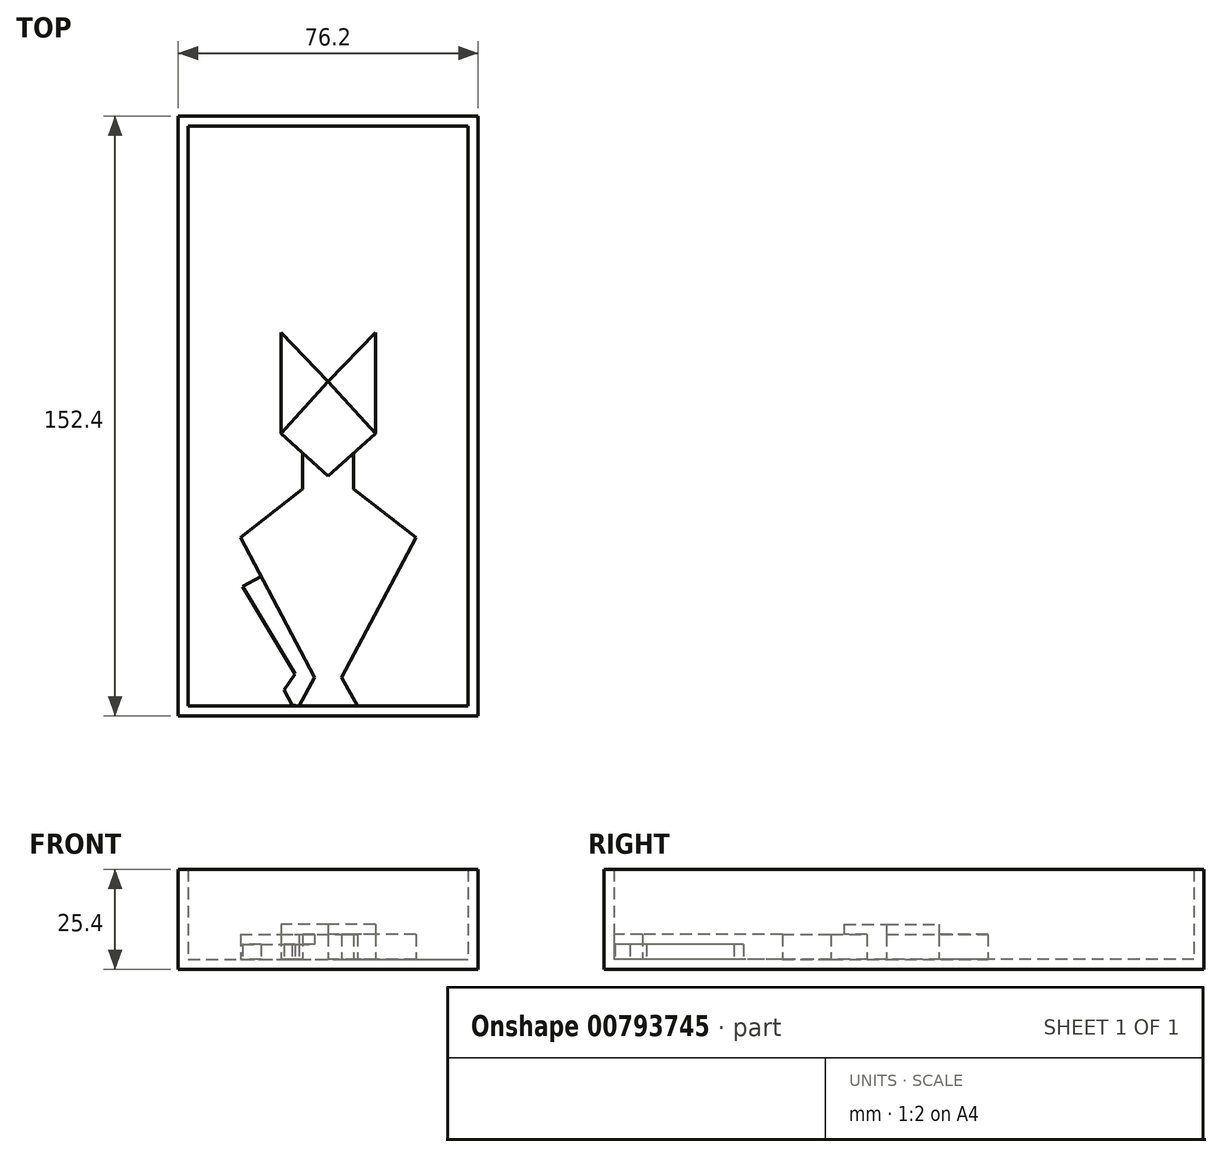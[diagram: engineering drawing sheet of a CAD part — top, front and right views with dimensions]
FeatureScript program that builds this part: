
annotation { "Feature Type Name" : "Feature", "Feature Type Description" : "" }
export const myFeature = defineFeature(function(context is Context, id is Id, definition is map)
    precondition{}
    {
        {
            var Q0;
            Q0=qCreatedBy(makeId("Top.planeOp"),FACE);
            var sketch = newSketch(context, id + "F0", { "sketchPlane" : qUnion([Q0])});
            skLineSegment(sketch, "E0.bottom", {"start": v(-38.1, 152.4) * mm, "end": v(38.1, 152.4) * mm});
            skLineSegment(sketch, "E0.top", {"start": v(-38.1, 0) * mm, "end": v(38.1, 0) * mm});
            skLineSegment(sketch, "E0.left", {"start": v(-38.1, 152.4) * mm, "end": v(-38.1, 0) * mm});
            skLineSegment(sketch, "E0.right", {"start": v(38.1, 152.4) * mm, "end": v(38.1, 0) * mm});
            skSolve(sketch);
        }
        {
            var Q0;
            Q0=makeQuery(id+"F0.imprint","IMPRINT",FACE,{"disambiguationData":[TD([[makeQuery(id+"F0.imprint","IMPRINT",EDGE,{"derivedFrom":sQuery(id+"F0.wireOp",EDGE,"E0.bottom")}),-1.0]])]});
            extrude(context, id + "F1", {"entities" : qUnion([Q0]), "depth" : 25.4 * mm, "offsetDistance" : 25.4 * mm});
        }
        {
            var Q0;
            Q0=makeQuery(id+"F1.opExtrude","CAP_FACE",FACE,{"disambiguationData":[OSD([sQuery(id+"F0.wireOp",EDGE,"E0.bottom"),sQuery(id+"F0.wireOp",EDGE,"E0.top"),sQuery(id+"F0.wireOp",EDGE,"E0.left"),sQuery(id+"F0.wireOp",EDGE,"E0.right")])],"isStart":false});
            shell(context, id + "F2", {"entities" : qUnion([Q0]), "thickness" : 2.54 * mm});
        }
        {
            var Q0;
            Q0=makeQuery(id+"F2.opShell","OFFSET_FACE",FACE,{"disambiguationData":[OSD([sQuery(id+"F0.wireOp",EDGE,"E0.bottom"),sQuery(id+"F0.wireOp",EDGE,"E0.top"),sQuery(id+"F0.wireOp",EDGE,"E0.left"),sQuery(id+"F0.wireOp",EDGE,"E0.right")])]});
            var sketch = newSketch(context, id + "F3", { "sketchPlane" : qUnion([Q0])});
            skPoint(sketch, "E1.startSnap0", {"position": v(0, 2.54) * mm});
            skLineSegment(sketch, "E2", {"start": v(-22.28, 45.28) * mm, "end": v(-6.5, 57.68) * mm});
            skLineSegment(sketch, "E3", {"start": v(-6.5, 57.68) * mm, "end": v(-6.5, 66.82) * mm});
            skLineSegment(sketch, "E4", {"start": v(-6.5, 66.82) * mm, "end": v(0, 60.94) * mm});
            skLineSegment(sketch, "E5.MirrorCS", {"start": v(6.5, 66.82) * mm, "end": v(0, 60.94) * mm});
            skLineSegment(sketch, "E6.MirrorCS", {"start": v(6.5, 57.68) * mm, "end": v(6.5, 66.82) * mm});
            skLineSegment(sketch, "E7.MirrorCS", {"start": v(22.28, 45.28) * mm, "end": v(6.5, 57.68) * mm});
            skLineSegment(sketch, "E8", {"start": v(-22.28, 45.28) * mm, "end": v(-3.45, 9.72) * mm});
            skLineSegment(sketch, "E9", {"start": v(-3.45, 9.72) * mm, "end": v(-7.4, 2.54) * mm});
            skLineSegment(sketch, "E10.MirrorCS", {"start": v(22.28, 45.28) * mm, "end": v(3.45, 9.72) * mm});
            skLineSegment(sketch, "E11.MirrorCS", {"start": v(3.45, 9.72) * mm, "end": v(7.4, 2.54) * mm});
            skLineSegment(sketch, "E12", {"start": v(-7.4, 2.54) * mm, "end": v(7.4, 2.54) * mm});
            skSolve(sketch);
        }
        {
            var Q0;
            Q0=makeQuery(id+"F3.imprint","IMPRINT",FACE,{"disambiguationData":[TD([[makeQuery(id+"F3.imprint","IMPRINT",EDGE,{"derivedFrom":sQuery(id+"F3.wireOp",EDGE,"E2")}),-1.0]])]});
            extrude(context, id + "F4", {"entities" : qUnion([Q0]), "operationType" : NewBodyOperationType.ADD, "depth" : 6.35 * mm, "offsetDistance" : 25.4 * mm});
        }
        {
            var Q0;
            Q0=makeQuery(id+"F2.opShell","OFFSET_FACE",FACE,{"disambiguationData":[OSD([sQuery(id+"F0.wireOp",EDGE,"E0.bottom"),sQuery(id+"F0.wireOp",EDGE,"E0.top"),sQuery(id+"F0.wireOp",EDGE,"E0.left"),sQuery(id+"F0.wireOp",EDGE,"E0.right")])]});
            var sketch = newSketch(context, id + "F5", { "sketchPlane" : qUnion([Q0])});
            skLineSegment(sketch, "E13", {"start": v(0, 60.94) * mm, "end": v(-11.98, 71.78) * mm});
            skLineSegment(sketch, "E14", {"start": v(-11.98, 71.78) * mm, "end": v(0, 85.02) * mm});
            skLineSegment(sketch, "E15.MirrorCS", {"start": v(11.98, 71.78) * mm, "end": v(0, 85.02) * mm});
            skLineSegment(sketch, "E16.MirrorCS", {"start": v(0, 60.94) * mm, "end": v(11.98, 71.78) * mm});
            skSolve(sketch);
        }
        {
            var Q0;
            {var subQ1=sQuery(id+"F5.wireOp",EDGE,"E14");Q0=makeQuery(id+"F5.imprint","IMPRINT",FACE,{"disambiguationData":[TD([[makeQuery(id+"F5.imprint","IMPRINT",EDGE,{"derivedFrom":subQ1}),-1.0]])]});}
            extrude(context, id + "F6", {"entities" : qUnion([Q0]), "operationType" : NewBodyOperationType.ADD, "depth" : 8.9 * mm, "offsetDistance" : 25.4 * mm});
        }
        {
            var Q0;
            Q0=makeQuery(id+"F2.opShell","OFFSET_FACE",FACE,{"disambiguationData":[OSD([sQuery(id+"F0.wireOp",EDGE,"E0.bottom"),sQuery(id+"F0.wireOp",EDGE,"E0.top"),sQuery(id+"F0.wireOp",EDGE,"E0.left"),sQuery(id+"F0.wireOp",EDGE,"E0.right")])]});
            var sketch = newSketch(context, id + "F7", { "sketchPlane" : qUnion([Q0])});
            skLineSegment(sketch, "E17", {"start": v(-11.98, 71.78) * mm, "end": v(-11.98, 97.46) * mm});
            skLineSegment(sketch, "E18", {"start": v(-11.98, 97.46) * mm, "end": v(0, 85.02) * mm});
            skLineSegment(sketch, "E19.MirrorCS", {"start": v(11.98, 97.46) * mm, "end": v(0, 85.02) * mm});
            skLineSegment(sketch, "E20.MirrorCS", {"start": v(11.98, 71.78) * mm, "end": v(11.98, 97.46) * mm});
            skSolve(sketch);
        }
        {
            var Q0;
            Q0=makeQuery(id+"F7.imprint","IMPRINT",FACE,{"disambiguationData":[TD([[makeQuery(id+"F7.imprint","IMPRINT",EDGE,{"derivedFrom":sQuery(id+"F7.wireOp",EDGE,"E19.MirrorCS")}),1.0]])]});
            var Q1;
            Q1=makeQuery(id+"F7.imprint","IMPRINT",FACE,{"disambiguationData":[TD([[makeQuery(id+"F7.imprint","IMPRINT",EDGE,{"derivedFrom":sQuery(id+"F7.wireOp",EDGE,"E17")}),-1.0]])]});
            extrude(context, id + "F8", {"entities" : qUnion([Q0, Q1]), "operationType" : NewBodyOperationType.ADD, "depth" : 6.35 * mm, "offsetDistance" : 25.4 * mm});
        }
        {
            var Q0;
            Q0=makeQuery(id+"F7.imprint","IMPRINT",FACE,{"disambiguationData":[TD([[makeQuery(id+"F7.imprint","IMPRINT",EDGE,{"derivedFrom":sQuery(id+"F7.wireOp",EDGE,"E17")}),1.0]])]});
            var sketch = newSketch(context, id + "F9", { "sketchPlane" : qUnion([Q0])});
            skLineSegment(sketch, "E21.0", {"start": v(-17.06, 35.42) * mm, "end": v(-3.45, 9.72) * mm});
            skLineSegment(sketch, "E22.0", {"start": v(-3.45, 9.72) * mm, "end": v(-7.4, 2.54) * mm});
            skLineSegment(sketch, "E23", {"start": v(-17.06, 35.42) * mm, "end": v(-21.77, 32.93) * mm});
            skLineSegment(sketch, "E24", {"start": v(-21.77, 32.93) * mm, "end": v(-8.37, 10.7) * mm});
            skLineSegment(sketch, "E25", {"start": v(-8.37, 10.7) * mm, "end": v(-11.24, 6.57) * mm});
            skLineSegment(sketch, "E26", {"start": v(-11.24, 6.57) * mm, "end": v(-9.22, 2.77) * mm});
            skLineSegment(sketch, "E27", {"start": v(-9.22, 2.77) * mm, "end": v(-7.4, 2.54) * mm});
            skLineSegment(sketch, "E28.0.0", {"start": v(11.98, 97.46) * mm, "end": v(11.98, 71.78) * mm});
            skLineSegment(sketch, "E28.0.1", {"start": v(11.98, 71.78) * mm, "end": v(6.5, 66.82) * mm});
            skLineSegment(sketch, "E28.0.2", {"start": v(6.5, 66.82) * mm, "end": v(6.5, 57.68) * mm});
            skLineSegment(sketch, "E28.0.3", {"start": v(6.5, 57.68) * mm, "end": v(22.28, 45.28) * mm});
            skLineSegment(sketch, "E28.0.4", {"start": v(22.28, 45.28) * mm, "end": v(3.45, 9.72) * mm});
            skLineSegment(sketch, "E28.0.5", {"start": v(3.45, 9.72) * mm, "end": v(7.4, 2.54) * mm});
            skLineSegment(sketch, "E28.0.6", {"start": v(7.4, 2.54) * mm, "end": v(35.56, 2.54) * mm});
            skLineSegment(sketch, "E28.0.7", {"start": v(35.56, 2.54) * mm, "end": v(35.56, 149.86) * mm});
            skLineSegment(sketch, "E28.0.8", {"start": v(35.56, 149.86) * mm, "end": v(-35.56, 149.86) * mm});
            skLineSegment(sketch, "E28.0.9", {"start": v(-35.56, 149.86) * mm, "end": v(-35.56, 2.54) * mm});
            skLineSegment(sketch, "E28.0.10", {"start": v(-35.56, 2.54) * mm, "end": v(-7.4, 2.54) * mm});
            skLineSegment(sketch, "E28.0.11", {"start": v(-7.4, 2.54) * mm, "end": v(-3.45, 9.72) * mm});
            skLineSegment(sketch, "E28.0.12", {"start": v(-3.45, 9.72) * mm, "end": v(-17.06, 35.42) * mm});
            skLineSegment(sketch, "E28.0.13", {"start": v(-22.28, 45.28) * mm, "end": v(-6.5, 57.68) * mm});
            skLineSegment(sketch, "E28.0.14", {"start": v(-6.5, 57.68) * mm, "end": v(-6.5, 66.82) * mm});
            skLineSegment(sketch, "E28.0.15", {"start": v(-6.5, 66.82) * mm, "end": v(-11.98, 71.78) * mm});
            skLineSegment(sketch, "E28.0.16", {"start": v(-11.98, 71.78) * mm, "end": v(-11.98, 97.46) * mm});
            skLineSegment(sketch, "E28.0.17", {"start": v(-11.98, 97.46) * mm, "end": v(0, 85.02) * mm});
            skLineSegment(sketch, "E28.0.18", {"start": v(0, 85.02) * mm, "end": v(11.98, 97.46) * mm});
            skPoint(sketch, "E29.orphan", {"position": v(-22.28, 45.28) * mm});
            skSolve(sketch);
        }
        {
            var Q0;
            Q0 = qSketchRegion(id + "F9", true);
            extrude(context, id + "F10", {"entities" : qUnion([Q0]), "operationType" : NewBodyOperationType.ADD, "depth" : 3.8 * mm, "offsetDistance" : 25.4 * mm});
        }
    });
